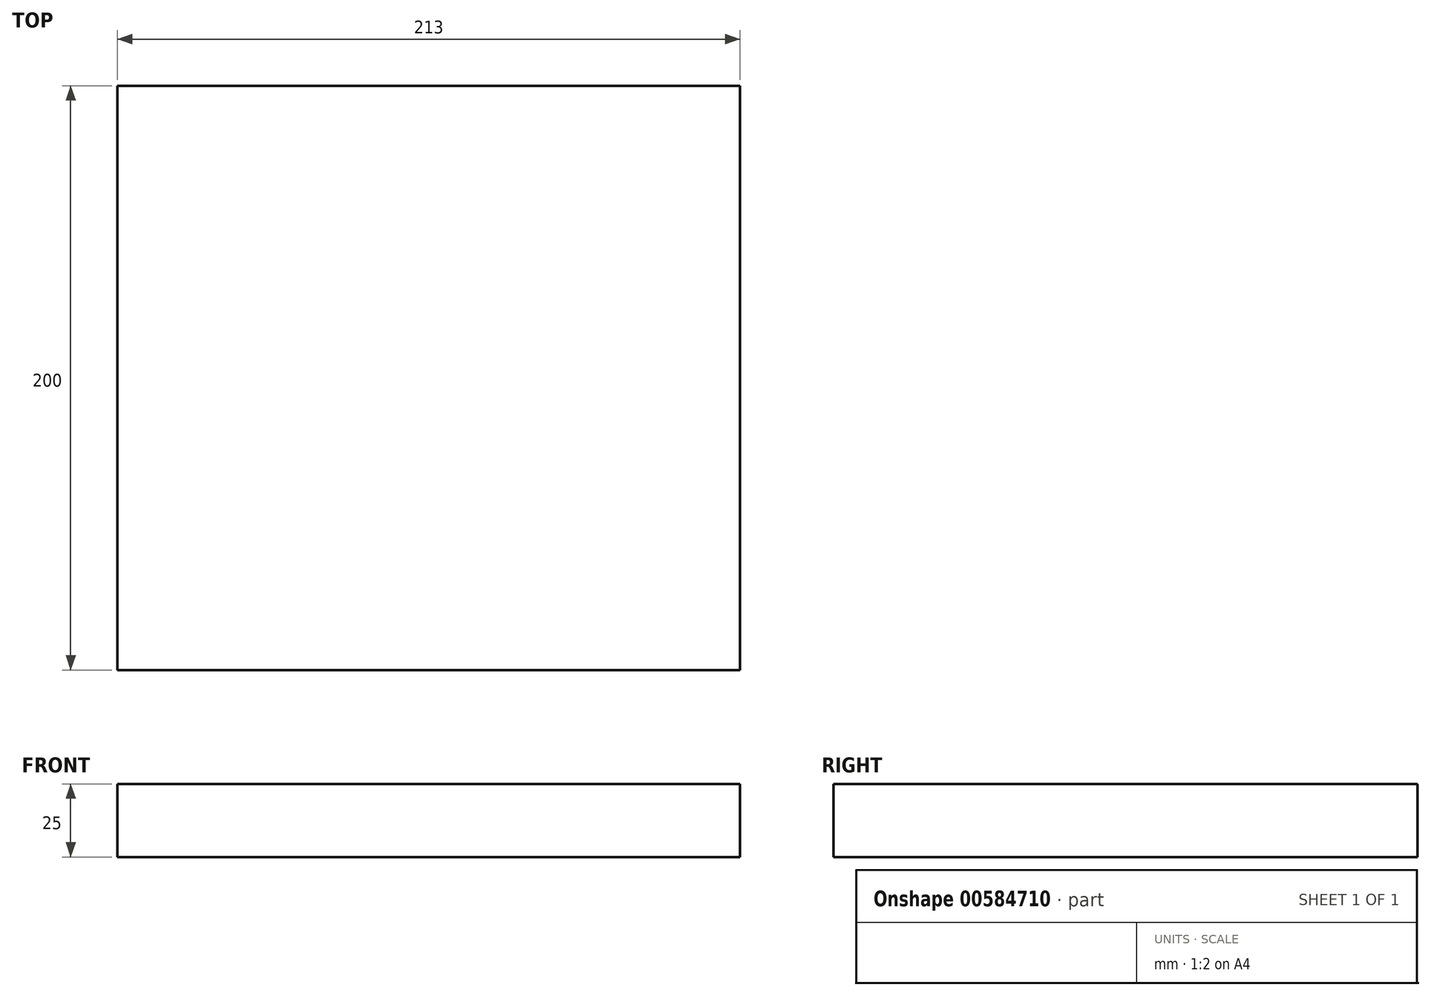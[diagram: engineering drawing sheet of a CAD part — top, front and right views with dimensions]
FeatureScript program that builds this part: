
annotation { "Feature Type Name" : "Feature", "Feature Type Description" : "" }
export const myFeature = defineFeature(function(context is Context, id is Id, definition is map)
    precondition{}
    {
        {
            var Q0;
            Q0=qCreatedBy(makeId("Top.planeOp"),FACE);
            var sketch = newSketch(context, id + "F0", { "sketchPlane" : qUnion([Q0])});
            skLineSegment(sketch, "E0.bottom", {"start": v(106.5, -100) * mm, "end": v(-106.5, -100) * mm});
            skLineSegment(sketch, "E0.top", {"start": v(106.5, 100) * mm, "end": v(-106.5, 100) * mm});
            skLineSegment(sketch, "E0.left", {"start": v(106.5, -100) * mm, "end": v(106.5, 100) * mm});
            skLineSegment(sketch, "E0.right", {"start": v(-106.5, -100) * mm, "end": v(-106.5, 100) * mm});
            skPoint(sketch, "E0.middle", {"position": v(0, 0) * mm});
            skSolve(sketch);
        }
        {
            var Q0;
            Q0 = qSketchRegion(id + "F0", true);
            extrude(context, id + "F1", {"entities" : qUnion([Q0]), "depth" : 25 * mm, "offsetDistance" : 25 * mm});
        }
    });
